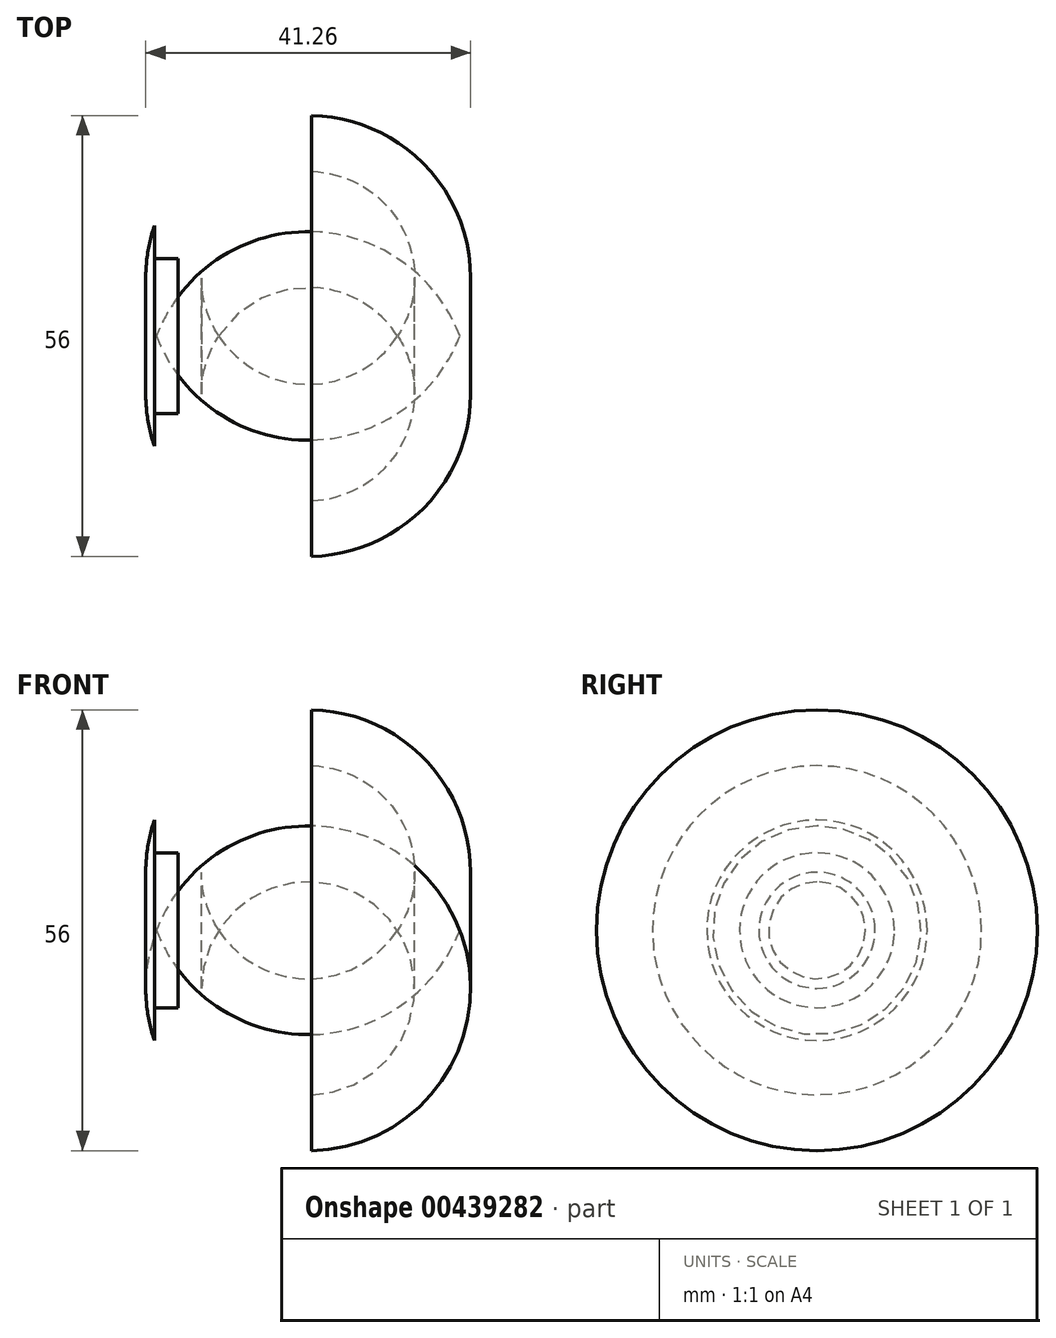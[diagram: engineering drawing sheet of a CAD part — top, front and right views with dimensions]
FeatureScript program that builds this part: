
annotation { "Feature Type Name" : "Feature", "Feature Type Description" : "" }
export const myFeature = defineFeature(function(context is Context, id is Id, definition is map)
    precondition{}
    {
        {
            var Q0;
            Q0=qCreatedBy(makeId("Front.planeOp"),FACE);
            var sketch = newSketch(context, id + "F0", { "sketchPlane" : qUnion([Q0])});
            skLineSegment(sketch, "E0.bottom", {"start": v(20, 28) * mm, "end": v(0, 28) * mm, "construction": true});
            skLineSegment(sketch, "E0.top", {"start": v(20, 0) * mm, "end": v(0, 0) * mm, "construction": true});
            skLineSegment(sketch, "E0.left", {"start": v(20, 28) * mm, "end": v(20, 0) * mm, "construction": true});
            skLineSegment(sketch, "E0.right", {"start": v(0, 28) * mm, "end": v(0, 0) * mm, "construction": true});
            skLineSegment(sketch, "E1", {"start": v(0, 0) * mm, "end": v(3, 0) * mm, "construction": true});
            skLineSegment(sketch, "E2", {"start": v(3, 0) * mm, "end": v(3, 9.84) * mm});
            skLineSegment(sketch, "E3", {"start": v(3, 0) * mm, "end": v(6, 0) * mm});
            skLineSegment(sketch, "E4", {"start": v(6, 0) * mm, "end": v(6, 7.38) * mm});
            skLineSegment(sketch, "E5", {"start": v(3, 9.84) * mm, "end": v(0, 9.84) * mm});
            skLineSegment(sketch, "E6", {"start": v(0, 9.84) * mm, "end": v(0, 14) * mm});
            skArc(sketch, "E7", {"start": v(20, 28) * mm, "mid": v(7.7, 24.28) * mm, "end": v(0, 14) * mm});
            skLineSegment(sketch, "E8", {"start": v(20, 28) * mm, "end": v(20, 20.9) * mm});
            skArc(sketch, "E9", {"start": v(20, 20.9) * mm, "mid": v(10.13, 17.11) * mm, "end": v(6, 7.38) * mm});
            skSolve(sketch);
        }
        {
            var Q0;
            Q0=makeQuery(id+"F0.imprint","IMPRINT",FACE,{"disambiguationData":[TD([[makeQuery(id+"F0.imprint","IMPRINT",EDGE,{"derivedFrom":sQuery(id+"F0.wireOp",EDGE,"E2")}),-1.0]])]});
            var Q1;
            Q1=sQuery(id+"F0.wireOp",EDGE,"E0.top");
            revolve(context, id + "F1", {"entities" : qUnion([Q0]), "axis" : qUnion([Q1]), "revolveType" : RevolveType.FULL});
        }
    });
